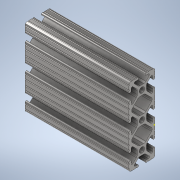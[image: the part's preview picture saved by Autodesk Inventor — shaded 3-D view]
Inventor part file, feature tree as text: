
AUTODESK INVENTOR PART (.ipt)
format: ipt  version: 2020 (Build 240168000, 168)  size: 372,736 bytes
history: native  units: in
note: dims shown in document units (in); Inventor stores cm internally (conversion verified against a paired STEP export)
features: sketch x2, extrude x1
ambient origin geometry x8: Origin, YZ Plane, XZ Plane, XY Plane, X Axis, Y Axis, Z Axis, Center Point
bodies: Solid1 (feature_tree)
feature tree (3):
  extrude  "Extrusion1"  [1 undecoded]
  sketch  "Sketch2"
  sketch  "Sketch1"  dims[d0=4.0in d1=0.0in]
note: 1 required parameter value undecoded (feature->parameter linkage not recoverable at this tier; creation-order binding heuristic only, values carry confidence <= 0.55)
